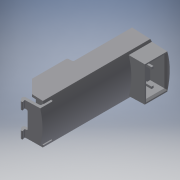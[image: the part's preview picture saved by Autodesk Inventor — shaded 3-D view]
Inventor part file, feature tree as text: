
AUTODESK INVENTOR PART (.ipt)
format: ipt  version: 2017.1 (Build 211199000, 199)  size: 414,720 bytes
history: native  units: mm
features: sketch x26, extrude x22, other x14, revolve x4
ambient origin geometry x8: Origin, YZ Plane, XZ Plane, XY Plane, X Axis, Y Axis, Z Axis, Center Point
bodies: Solid1 (feature_tree)
feature tree (66):
  extrude  "Extrusion1"  Depth=10.0mm TaperAngle=0.0deg
  sketch  "Sketch_1"  dims[d0=10.0mm d1=0.0mm d2=2.0mm d3=0.0mm]
  sketch  "Sketch_3"  dims[d7=0.77mm d8=0.0mm d9=0.77mm d10=0.0mm]
  extrude  "Extrusion2"  Depth=7.0mm TaperAngle=0.0deg
  revolve  "Revolution1"  [1 undecoded]
  sketch  "Sketch_6"  dims[d19=30.0mm d20=0.0mm d21=5.0mm d22=0.0mm]
  sketch  "Sketch_7"  dims[d23=35.0mm d24=0.0mm d25=1.5mm d26=0.0mm]
  extrude  "Extrusion3"  Depth=10.0mm TaperAngle=0.0deg
  extrude  "Extrusion4"  Depth=0.512mm TaperAngle=0.0deg
  extrude  "Extrusion5"  Depth=5.0mm TaperAngle=0.0deg
  extrude  "Extrusion6"  Depth=1.5mm TaperAngle=0.0deg
  extrude  "Extrusion7"  Depth=6.0mm
  extrude  "Extrusion8"  Depth=2.0mm TaperAngle=45.0deg
  extrude  "Extrusion9"  Depth=3.25mm TaperAngle=0.0deg
  extrude  "Extrusion10"  Depth=1.05mm
  extrude  "Extrusion11"  TaperAngle=360.0deg  [1 undecoded]
  extrude  "Extrusion12"  Depth=1.722mm TaperAngle=0.0deg
  extrude  "Extrusion13"  [1 undecoded]
  extrude  "Extrusion14"  [1 undecoded]
  extrude  "Extrusion15"  [1 undecoded]
  revolve  "Revolution2"  [1 undecoded]
  extrude  "Extrusion16"  [1 undecoded]
  extrude  "Extrusion17"  [1 undecoded]
  extrude  "Extrusion18"  [1 undecoded]
  extrude  "Extrusion19"  [1 undecoded]
  extrude  "Extrusion20"  [1 undecoded]
  extrude  "Extrusion21"  [1 undecoded]
  revolve  "Revolution3"  [1 undecoded]
  revolve  "Revolution4"  [1 undecoded]
  extrude  "Extrusion22"  [1 undecoded]
  other  "NEBV_XY"
  other  "NEBV_YZ"
  other  "NEBV_ZX"
  other  "NEBV_X"
  other  "NEBV_Y"
  other  "NEBV_Z"
  other  "NEBV_Center"
  other  "VAVE_XY"
  other  "VAVE_YZ"
  other  "VAVE_ZX"
  other  "VAVE_X"
  other  "VAVE_Y"
  other  "VAVE_Z"
  other  "VAVE_Center"
  sketch  "Sketch_23"
  sketch  "Sketch_4"  dims[d11=3.062mm d12=0.0mm d13=10.0mm d14=0.0mm]
  sketch  "Sketch_5"  dims[d15=0.512mm d16=0.0mm d17=0.512mm d18=0.0mm]
  sketch  "Sketch_12"  dims[d42=1.05mm d43=-0.174533mm d44=360.0deg]
  sketch  "Sketch_8"  dims[d27=0.3mm d28=0.0mm d29=6.0mm d30=0.174533mm]
  sketch  "Sketch_9"  dims[d31=6.981317mm d32=2.0mm d33=45.0deg]
  sketch  "Sketch_10"  dims[d34=3.38mm d35=0.0mm d36=3.25mm d37=0.0mm]
  sketch  "Sketch_15"
  sketch  "Sketch_13"  dims[d45=360.0deg d46=1.722mm d47=0.0mm]
  sketch  "Sketch_14"
  sketch  "Sketch_17"
  sketch  "Sketch_11"  dims[d38=3.25mm d39=0.0mm d40=1.05mm d41=-0.174533mm]
  sketch  "Sketch_16"
  sketch  "Sketch_19"
  sketch  "Sketch_20"
  sketch  "Sketch_21"
  sketch  "Sketch_22"
  sketch  "Sketch_2"  dims[d4=60.0deg d5=7.0mm d6=0.0mm]
  sketch  "Sketch_24"
  sketch  "Sketch_25"
  sketch  "Sketch_26"
  sketch  "Sketch_40"
note: 15 required parameter values undecoded (feature->parameter linkage not recoverable at this tier; creation-order binding heuristic only, values carry confidence <= 0.55)